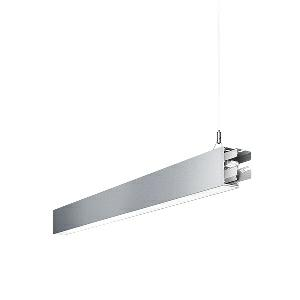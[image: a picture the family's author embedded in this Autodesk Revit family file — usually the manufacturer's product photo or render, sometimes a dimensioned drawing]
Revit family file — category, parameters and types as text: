
# Revit family: dotoo_line_-_dlp_2000_830_d_mid_00805849_c27c
name_source: partatom
category: Lighting Fixtures
units: mm (PartAtom-declared; Revit-internal decimal feet)

## family parameters
Cut with Voids When Loaded = No
Host = Face
Light Source = No
Part Type = Normal
Room Calculation Point = No
Round Connector Dimension = Use Diameter
Shared = No

## types (1)
- DOTOO.line - DLP 2000/830/D MID (1 x LED, 1650 lm, 3000K)
    Apparent Load = 16 VA
    Approval mark = CE
    CIE Flux Codes = 67 91 98 100 100
    Color Rendering = 80-89
    Color Temperature = 3000K
    Control Gear = Electronic ballast
    Default Elevation = 1800 mm
    Description = DLP 2000/830/D|Suspended luminaire|light source: LED|connected load: 220-240 V, 50/60 Hz|Power consumption: approx. 16 W|standby: approx. 0,15|luminous flux: 1650 lm|luminous efficacy: 103 lm/W|light distribution: Direct|direct ratio: approx. 100 %|colour temperature: Warm white, ca. 3000 K|color rendering index (CRI): >= 80|chromaticity tolerance:  3 SDCM|System of protection: IP 40|technology: Continuously dimmable|luminaire body|material: Sectional aluminium|colour: Silver|lamp cover: Acrylic (PMMA), Clear|mains lead: 1,0 m With free stranded wires|Fastening: Steel cable 0.3 - 0.7 m|glare control: Prism aperture|luminance(L65): <= 3000 cd/m|unified glare rating(4H 8H): <=  19|special features: DALI Load 1x, TouchDIM - dimming via standard switch, Through-wired, up to 18 m on one mains connection, Flicker-free, Suitable as emergency lighting, Mechanical and electrical connection of the individual modules without tools|
    Frequency = 50 Hz
    Height = 110 mm
    Lamp = 1 x LED
    Lamp Light Flux = 1650 lm
    Lamp count = 1
    Length = 1402 mm
    Luminous efficacy = 103 lm/W
    Manufacturer = Waldmann
    ModVariant = No
    Model = 00805849
    Mounting Place = Ceiling
    Mounting Type = Pendant
    Number of Poles = 1
    OnlyDefault = Yes
    Power Factor = 1
    Product Name = DOTOO.line - DLP 2000/830/D MID
    Product group = Suspended luminaire
    ProductGroupID = 9
    Protection Class = Protection class I
    Protection Degree = IP 40
    RLX_Detail_Level = 1
    RLX_Emergency_Light_Flux = 0 lm
    RLX_Emergency_Type = 0
    RLX_Emergency_Type_DB = No
    RlxData = <blob elided: 21981 chars, md5=91e7de97>
    Socket = socket
    Standby Power = 0 W
    System Light Flux = 1650 lm
    System Power = 16 W
    Type Comments = Product without accessories
    Type Image = 113311000-00692597.jpg
    URL = http://relux.com
    VarID = ---
    Voltage = 230 V
    Voltage Range = 220-240 V
    Weight = 0.00 kg
    Width = 60 mm  [stored 0.19685 ft]

note: [stored X ft] marks values corroborated as IEEE doubles in the binary element streams (Revit-internal decimal feet)

## geometry (parser evidence)
native form markers: Blend x4, Sweep x13
no freeform markers — native parametric forms only
